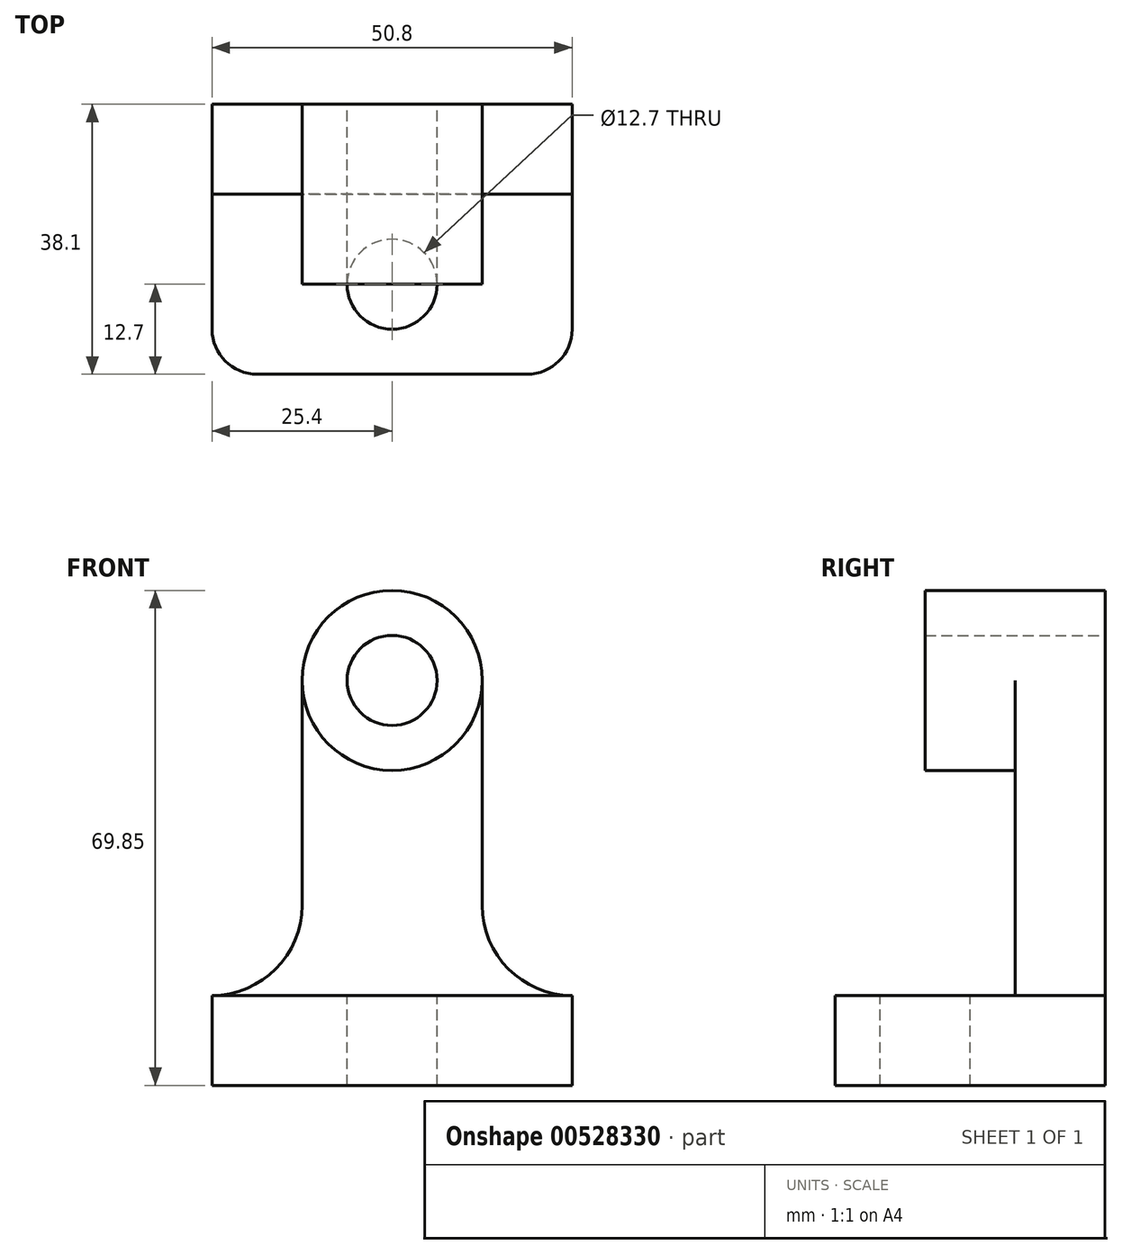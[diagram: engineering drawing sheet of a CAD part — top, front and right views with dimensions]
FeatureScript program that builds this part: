
annotation { "Feature Type Name" : "Feature", "Feature Type Description" : "" }
export const myFeature = defineFeature(function(context is Context, id is Id, definition is map)
    precondition{}
    {
        {
            var Q0;
            Q0=qCreatedBy(makeId("Front.planeOp"),FACE);
            var sketch = newSketch(context, id + "F0", { "sketchPlane" : qUnion([Q0])});
            skLineSegment(sketch, "E0", {"start": v(0, 0) * mm, "end": v(0, -12.7) * mm});
            skLineSegment(sketch, "E1", {"start": v(0, -12.7) * mm, "end": v(-50.8, -12.7) * mm});
            skLineSegment(sketch, "E2", {"start": v(-50.8, -12.7) * mm, "end": v(-50.8, 0) * mm});
            skLineSegment(sketch, "E3", {"start": v(-50.8, 0) * mm, "end": v(0, 0) * mm});
            skSolve(sketch);
        }
        {
            var Q0;
            Q0 = qSketchRegion(id + "F0", true);
            extrude(context, id + "F1", {"entities" : qUnion([Q0]), "depth" : 38.1 * mm, "offsetDistance" : 25.4 * mm});
        }
        {
            var Q0;
            Q0=makeQuery(id+"F1.opExtrude","CAP_FACE",FACE,{"disambiguationData":[OSD([sQuery(id+"F0.wireOp",EDGE,"E0"),sQuery(id+"F0.wireOp",EDGE,"E1"),sQuery(id+"F0.wireOp",EDGE,"E2"),sQuery(id+"F0.wireOp",EDGE,"E3")])],"isStart":true});
            var sketch = newSketch(context, id + "F2", { "sketchPlane" : qUnion([Q0])});
            skLineSegment(sketch, "E4", {"start": v(0, 0) * mm, "end": v(12.7, 0) * mm, "construction": true});
            skLineSegment(sketch, "E5", {"start": v(12.7, 0) * mm, "end": v(38.1, 0) * mm, "construction": true});
            skLineSegment(sketch, "E6", {"start": v(38.1, 0) * mm, "end": v(50.8, 0) * mm, "construction": true});
            skLineSegment(sketch, "E7", {"start": v(12.7, 44.45) * mm, "end": v(38.1, 44.45) * mm, "construction": true});
            skCircle(sketch, "E8", {"center": v(25.4, 44.45) * mm, "radius": 12.7 * mm});
            skCircle(sketch, "E9", {"center": v(25.4, 44.45) * mm, "radius": 6.35 * mm});
            skLineSegment(sketch, "E10", {"start": v(12.7, 0) * mm, "end": v(12.7, 12.7) * mm, "construction": true});
            skLineSegment(sketch, "E11", {"start": v(12.7, 12.7) * mm, "end": v(12.7, 44.45) * mm});
            skLineSegment(sketch, "E12", {"start": v(38.1, 44.45) * mm, "end": v(38.1, 12.7) * mm});
            skLineSegment(sketch, "E13", {"start": v(38.1, 12.7) * mm, "end": v(38.1, 0) * mm, "construction": true});
            skArc(sketch, "E14", {"start": v(0, 0) * mm, "mid": v(8.98, 3.72) * mm, "end": v(12.7, 12.7) * mm});
            skArc(sketch, "E15", {"start": v(38.1, 12.7) * mm, "mid": v(41.82, 3.72) * mm, "end": v(50.8, 0) * mm});
            skSolve(sketch);
        }
        {
            var Q0;
            {var subQ1=sQuery(id+"F2.wireOp",EDGE,"E11");Q0=makeQuery(id+"F2.imprint","IMPRINT",FACE,{"disambiguationData":[TD([[makeQuery(id+"F2.imprint","IMPRINT",EDGE,{"derivedFrom":subQ1}),-1.0]])]});}
            extrude(context, id + "F3", {"entities" : qUnion([Q0]), "operationType" : NewBodyOperationType.ADD, "oppositeDirection" : true, "depth" : 12.7 * mm, "offsetDistance" : 25.4 * mm});
        }
        {
            var Q0;
            Q0=makeQuery(id+"F2.imprint","IMPRINT",FACE,{"disambiguationData":[TD([[makeQuery(id+"F2.imprint","IMPRINT",EDGE,{"derivedFrom":sQuery(id+"F2.wireOp",EDGE,"E9")}),-1.0]])]});
            extrude(context, id + "F4", {"entities" : qUnion([Q0]), "operationType" : NewBodyOperationType.ADD, "oppositeDirection" : true, "depth" : 25.4 * mm, "offsetDistance" : 25.4 * mm});
        }
        {
            var Q0;
            Q0=makeQuery(id+"F1.opExtrude","SWEPT_FACE",FACE,{"disambiguationData":[OSD([sQuery(id+"F0.wireOp",EDGE,"E3")])]});
            var sketch = newSketch(context, id + "F5", { "sketchPlane" : qUnion([Q0])});
            skLineSegment(sketch, "E16", {"start": v(-50.8, -38.1) * mm, "end": v(-25.4, -38.1) * mm, "construction": true});
            skLineSegment(sketch, "E17", {"start": v(-25.4, -38.1) * mm, "end": v(-25.4, -25.4) * mm, "construction": true});
            skCircle(sketch, "E18", {"center": v(-25.4, -25.4) * mm, "radius": 6.35 * mm});
            skSolve(sketch);
        }
        {
            var Q0;
            Q0=makeQuery(id+"F5.imprint","IMPRINT",FACE,{"disambiguationData":[TD([[makeQuery(id+"F5.imprint","IMPRINT",EDGE,{"derivedFrom":sQuery(id+"F5.wireOp",EDGE,"E18")}),1.0]])]});
            extrude(context, id + "F6", {"entities" : qUnion([Q0]), "operationType" : NewBodyOperationType.REMOVE, "endBound" : BoundingType.THROUGH_ALL, "oppositeDirection" : true, "depth" : 25.4 * mm, "offsetDistance" : 25.4 * mm});
        }
        {
            var Q0;
            Q0=makeQuery(id+"F1.opExtrude","CAP_EDGE",EDGE,{"disambiguationData":[OSD([sQuery(id+"F0.wireOp",EDGE,"E2")])],"isStart":false});
            var Q1;
            Q1=makeQuery(id+"F1.opExtrude","CAP_EDGE",EDGE,{"disambiguationData":[OSD([sQuery(id+"F0.wireOp",EDGE,"E0")])],"isStart":false});
            fillet(context, id + "F7", {"entities" : qUnion([Q0, Q1]), "radius" : 6.35 * mm, "tangentPropagation" : true, "allowEdgeOverflow" : false});
        }
    });
